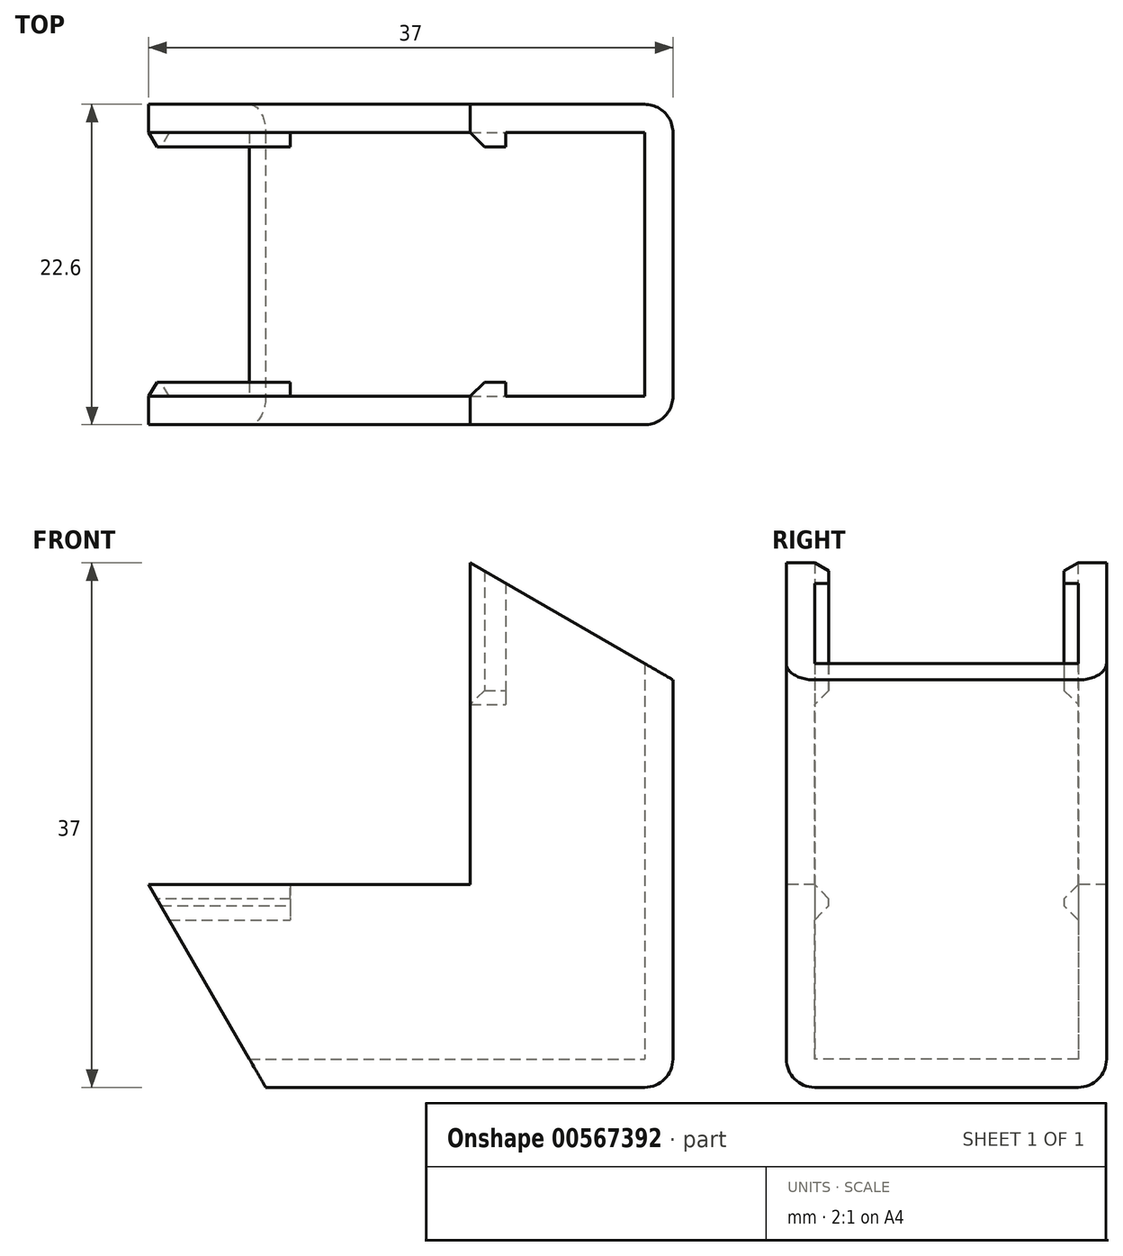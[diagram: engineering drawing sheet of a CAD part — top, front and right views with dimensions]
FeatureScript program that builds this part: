
annotation { "Feature Type Name" : "Feature", "Feature Type Description" : "" }
export const myFeature = defineFeature(function(context is Context, id is Id, definition is map)
    precondition{}
    {
        {
            assignVariable(context, id + "F0", {"name" : "Thickness", "anyValue" : 2});
        }
        {
            assignVariable(context, id + "F1", {"name" : "InsideWidth", "anyValue" : 18.6});
        }
        {
            assignVariable(context, id + "F2", {"name" : "OutsideLength", "anyValue" : 37});
        }
        {
            assignVariable(context, id + "F3", {"name" : "InsideDepth", "anyValue" : 12.3});
        }
        {
            var Q0;
            Q0=qCreatedBy(makeId("Top.planeOp"),FACE);
            var sketch = newSketch(context, id + "F4", { "sketchPlane" : qUnion([Q0])});
            skLineSegment(sketch, "E0.bottom", {"start": v(0, 0) * mm, "end": v(35, 0) * mm});
            skLineSegment(sketch, "E0.top", {"start": v(0, -22.6) * mm, "end": v(35, -22.6) * mm});
            skLineSegment(sketch, "E0.left", {"start": v(0, 0) * mm, "end": v(0, -22.6) * mm});
            skLineSegment(sketch, "E0.right", {"start": v(35, 0) * mm, "end": v(35, -22.6) * mm});
            skLineSegment(sketch, "E1.bottom", {"start": v(35, 0) * mm, "end": v(37, 0) * mm});
            skLineSegment(sketch, "E1.top", {"start": v(35, -22.6) * mm, "end": v(37, -22.6) * mm});
            skLineSegment(sketch, "E1.right", {"start": v(37, 0) * mm, "end": v(37, -22.6) * mm});
            skLineSegment(sketch, "E2", {"start": v(0, -11.3) * mm, "end": v(37, -11.3) * mm, "construction": true});
            skLineSegment(sketch, "E3", {"start": v(37, -2) * mm, "end": v(0, -2) * mm});
            skLineSegment(sketch, "E4", {"start": v(0, -20.6) * mm, "end": v(37, -20.6) * mm});
            skSolve(sketch);
        }
        {
            var Q0;
            {var subQ0=sQuery(id+"F4.wireOp",EDGE,"E3");var subQ1=sQuery(id+"F4.wireOp",EDGE,"E0.left");var subQ2=makeQuery(id+"F4.imprint","INTERSECT",VERTEX,{"derivedFrom":[subQ1,subQ0]});Q0=makeQuery(id+"F4.imprint","IMPRINT",FACE,{"disambiguationData":[TD([[makeQuery(id+"F4.imprint","IMPRINT",EDGE,{"disambiguationData":[TD([[subQ2,-1.0]])],"derivedFrom":subQ1}),1.0]])]});}
            extrude(context, id + "F5", {"entities" : qUnion([Q0]), "depth" : (getVariable(context, 'Thickness')) * mm, "offsetDistance" : 25 * mm});
        }
        {
            var Q0;
            {var subQ0=sQuery(id+"F4.wireOp",EDGE,"E3");var subQ1=sQuery(id+"F4.wireOp",EDGE,"E0.right");var subQ2=makeQuery(id+"F4.imprint","INTERSECT",VERTEX,{"derivedFrom":[subQ1,subQ0]});Q0=makeQuery(id+"F4.imprint","IMPRINT",FACE,{"disambiguationData":[TD([[makeQuery(id+"F4.imprint","IMPRINT",EDGE,{"disambiguationData":[TD([[subQ2,-1.0]])],"derivedFrom":subQ1}),1.0]])]});}
            var Q1;
            {var subQ0=sQuery(id+"F4.wireOp",EDGE,"E1.top");Q1=makeQuery(id+"F4.imprint","IMPRINT",FACE,{"disambiguationData":[TD([[makeQuery(id+"F4.imprint","IMPRINT",EDGE,{"derivedFrom":subQ0}),1.0]])]});}
            var Q2;
            {var subQ0=sQuery(id+"F4.wireOp",EDGE,"E1.bottom");Q2=makeQuery(id+"F4.imprint","IMPRINT",FACE,{"disambiguationData":[TD([[makeQuery(id+"F4.imprint","IMPRINT",EDGE,{"derivedFrom":subQ0}),-1.0]])]});}
            extrude(context, id + "F6", {"entities" : qUnion([Q0, Q1, Q2]), "operationType" : NewBodyOperationType.ADD, "depth" : (getVariable(context, 'OutsideLength')) * mm, "offsetDistance" : 25 * mm});
        }
        {
            var Q0;
            {var subQ0=sQuery(id+"F4.wireOp",EDGE,"E0.bottom");Q0=makeQuery(id+"F4.imprint","IMPRINT",FACE,{"disambiguationData":[TD([[makeQuery(id+"F4.imprint","IMPRINT",EDGE,{"derivedFrom":subQ0}),-1.0]])]});}
            var Q1;
            {var subQ0=sQuery(id+"F4.wireOp",EDGE,"E0.top");Q1=makeQuery(id+"F4.imprint","IMPRINT",FACE,{"disambiguationData":[TD([[makeQuery(id+"F4.imprint","IMPRINT",EDGE,{"derivedFrom":subQ0}),1.0]])]});}
            extrude(context, id + "F7", {"entities" : qUnion([Q0, Q1]), "operationType" : NewBodyOperationType.ADD, "depth" : (getVariable(context, 'InsideDepth') + getVariable(context, 'Thickness')) * mm, "offsetDistance" : 25 * mm});
        }
        {
            var Q0;
            Q0=makeQuery(id+"F6.opExtrude","SWEPT_FACE",FACE,{"disambiguationData":[OSD([sQuery(id+"F4.wireOp",EDGE,"E0.right")])]});
            var sketch = newSketch(context, id + "F8", { "sketchPlane" : qUnion([Q0])});
            skPoint(sketch, "E5.0", {"position": v(2, 14.3) * mm});
            skLineSegment(sketch, "E5.1", {"start": v(0, 14.3) * mm, "end": v(2, 14.3) * mm});
            skLineSegment(sketch, "E5.2", {"start": v(0, 37) * mm, "end": v(0, 14.3) * mm});
            skLineSegment(sketch, "E5.3", {"start": v(22.6, 37) * mm, "end": v(22.6, 14.3) * mm});
            skLineSegment(sketch, "E5.4", {"start": v(20.6, 14.3) * mm, "end": v(22.6, 14.3) * mm});
            skLineSegment(sketch, "E5.5", {"start": v(0, 37) * mm, "end": v(22.6, 37) * mm});
            skLineSegment(sketch, "E6", {"start": v(2, 14.3) * mm, "end": v(2, 37) * mm});
            skLineSegment(sketch, "E7", {"start": v(20.6, 14.3) * mm, "end": v(20.6, 37) * mm});
            skSolve(sketch);
        }
        {
            var Q0;
            Q0=makeQuery(id+"F8.imprint","IMPRINT",FACE,{"disambiguationData":[TD([[makeQuery(id+"F8.imprint","IMPRINT",EDGE,{"derivedFrom":sQuery(id+"F8.wireOp",EDGE,"E5.1")}),1.0]])]});
            var Q1;
            {var subQ0=sQuery(id+"F8.wireOp",EDGE,"E5.3");Q1=makeQuery(id+"F8.imprint","IMPRINT",FACE,{"disambiguationData":[TD([[makeQuery(id+"F8.imprint","IMPRINT",EDGE,{"derivedFrom":subQ0}),-1.0]])]});}
            extrude(context, id + "F9", {"entities" : qUnion([Q0, Q1]), "operationType" : NewBodyOperationType.ADD, "depth" : (getVariable(context, 'InsideDepth')) * mm, "offsetDistance" : 25 * mm});
        }
        {
            var Q0;
            Q0=makeQuery(id+"F9.boolean.opBoolean","MERGE",FACE,{"derivedFrom":[makeQuery(id+"F7.boolean.opBoolean","MERGE",FACE,{"derivedFrom":[makeQuery(id+"F6.opExtrude","SWEPT_FACE",FACE,{"disambiguationData":[OSD([sQuery(id+"F4.wireOp",EDGE,"E1.top")])]}),makeQuery(id+"F7.opExtrude","SWEPT_FACE",FACE,{"disambiguationData":[OSD([sQuery(id+"F4.wireOp",EDGE,"E0.top")])]})]}),makeQuery(id+"F9.opExtrude","SWEPT_FACE",FACE,{"disambiguationData":[OSD([sQuery(id+"F8.wireOp",EDGE,"E5.3")])]})]});
            var sketch = newSketch(context, id + "F10", { "sketchPlane" : qUnion([Q0])});
            skLineSegment(sketch, "E8", {"start": v(0, 14.3) * mm, "end": v(8.26, 0) * mm});
            skLineSegment(sketch, "E9", {"start": v(22.7, 37) * mm, "end": v(37, 28.74) * mm});
            skSolve(sketch);
        }
        {
            var Q0;
            {var subQ0=sQuery(id+"F10.wireOp",EDGE,"E8");Q0=makeQuery(id+"F10.imprint","IMPRINT",FACE,{"disambiguationData":[TD([[makeQuery(id+"F10.imprint","IMPRINT",EDGE,{"derivedFrom":subQ0}),-1.0]])]});}
            var Q1;
            {var subQ0=sQuery(id+"F10.wireOp",EDGE,"E9");Q1=makeQuery(id+"F10.imprint","IMPRINT",FACE,{"disambiguationData":[TD([[makeQuery(id+"F10.imprint","IMPRINT",EDGE,{"derivedFrom":subQ0}),1.0]])]});}
            extrude(context, id + "F11", {"entities" : qUnion([Q0, Q1]), "operationType" : NewBodyOperationType.REMOVE, "oppositeDirection" : true, "depth" : (getVariable(context, 'InsideWidth') + 2 * getVariable(context, 'Thickness')) * mm, "offsetDistance" : 25 * mm});
        }
        {
            var Q0;
            Q0=makeQuery(id+"F6.opExtrude","CAP_EDGE",EDGE,{"disambiguationData":[OSD([sQuery(id+"F4.wireOp",EDGE,"E1.right")])],"isStart":true});
            var Q1;
            Q1=makeQuery(id+"F7.boolean.opBoolean","MERGE",EDGE,{"derivedFrom":[makeQuery(id+"F6.opExtrude","CAP_EDGE",EDGE,{"disambiguationData":[OSD([sQuery(id+"F4.wireOp",EDGE,"E1.top")])],"isStart":true}),makeQuery(id+"F7.opExtrude","CAP_EDGE",EDGE,{"disambiguationData":[OSD([sQuery(id+"F4.wireOp",EDGE,"E0.top")])],"isStart":true})]});
            var Q2;
            Q2=makeQuery(id+"F6.opExtrude","SWEPT_EDGE",EDGE,{"disambiguationData":[OSD([sQuery(id+"F4.wireOp",EDGE,"E1.top"),sQuery(id+"F4.wireOp",EDGE,"E1.right")])]});
            var Q3;
            Q3=makeQuery(id+"F6.opExtrude","SWEPT_EDGE",EDGE,{"disambiguationData":[OSD([sQuery(id+"F4.wireOp",EDGE,"E1.bottom"),sQuery(id+"F4.wireOp",EDGE,"E1.right")])]});
            var Q4;
            Q4=makeQuery(id+"F7.boolean.opBoolean","MERGE",EDGE,{"derivedFrom":[makeQuery(id+"F6.opExtrude","CAP_EDGE",EDGE,{"disambiguationData":[OSD([sQuery(id+"F4.wireOp",EDGE,"E1.bottom")])],"isStart":true}),makeQuery(id+"F7.opExtrude","CAP_EDGE",EDGE,{"disambiguationData":[OSD([sQuery(id+"F4.wireOp",EDGE,"E0.bottom")])],"isStart":true})]});
            var Q5;
            Q5=makeQuery(id+"F11.boolean.opBoolean","COPY",EDGE,{"derivedFrom":makeQuery(id+"F11.opExtrude","SWEPT_EDGE",EDGE,{"disambiguationData":[OSD([sQuery(id+"F4.wireOp",EDGE,"E0.top"),sQuery(id+"F4.wireOp",EDGE,"E1.top"),sQuery(id+"F10.wireOp",EDGE,"E8")])]})});
            var Q6;
            Q6=makeQuery(id+"F11.boolean.opBoolean","COPY",EDGE,{"derivedFrom":makeQuery(id+"F11.opExtrude","SWEPT_EDGE",EDGE,{"disambiguationData":[OSD([sQuery(id+"F4.wireOp",EDGE,"E1.top"),sQuery(id+"F4.wireOp",EDGE,"E1.right"),sQuery(id+"F10.wireOp",EDGE,"E9")])]})});
            fillet(context, id + "F12", {"entities" : qUnion([Q0, Q1, Q2, Q3, Q4, Q5, Q6]), "radius" : (getVariable(context, 'Thickness')) * mm, "tangentPropagation" : true, "allowEdgeOverflow" : false});
        }
        {
            var Q0;
            Q0=makeQuery(id+"F9.boolean.opBoolean","MERGE",FACE,{"derivedFrom":[makeQuery(id+"F7.opExtrude","SWEPT_FACE",FACE,{"disambiguationData":[OSD([sQuery(id+"F4.wireOp",EDGE,"E3")])]}),makeQuery(id+"F9.opExtrude","SWEPT_FACE",FACE,{"disambiguationData":[OSD([sQuery(id+"F8.wireOp",EDGE,"E6")])]})]});
            var sketch = newSketch(context, id + "F13", { "sketchPlane" : qUnion([Q0])});
            skLineSegment(sketch, "E10.bottom", {"start": v(22.7, 37) * mm, "end": v(25.2, 37) * mm});
            skLineSegment(sketch, "E10.top", {"start": v(22.7, 27) * mm, "end": v(25.2, 27) * mm});
            skLineSegment(sketch, "E10.left", {"start": v(22.7, 37) * mm, "end": v(22.7, 27) * mm});
            skLineSegment(sketch, "E10.right", {"start": v(25.2, 37) * mm, "end": v(25.2, 27) * mm});
            skLineSegment(sketch, "E11.bottom", {"start": v(0, 14.3) * mm, "end": v(10, 14.3) * mm});
            skLineSegment(sketch, "E11.top", {"start": v(0, 11.8) * mm, "end": v(10, 11.8) * mm});
            skLineSegment(sketch, "E11.left", {"start": v(0, 14.3) * mm, "end": v(0, 11.8) * mm});
            skLineSegment(sketch, "E11.right", {"start": v(10, 14.3) * mm, "end": v(10, 11.8) * mm});
            skSolve(sketch);
        }
        {
            var Q0;
            {var subQ0=sQuery(id+"F13.wireOp",EDGE,"E10.top");Q0=makeQuery(id+"F13.imprint","IMPRINT",FACE,{"disambiguationData":[TD([[makeQuery(id+"F13.imprint","IMPRINT",EDGE,{"derivedFrom":subQ0}),1.0]])]});}
            var Q1;
            {var subQ0=sQuery(id+"F13.wireOp",EDGE,"E11.bottom");Q1=makeQuery(id+"F13.imprint","IMPRINT",FACE,{"disambiguationData":[TD([[makeQuery(id+"F13.imprint","IMPRINT",EDGE,{"derivedFrom":subQ0}),1.0]])]});}
            extrude(context, id + "F14", {"entities" : qUnion([Q0, Q1]), "operationType" : NewBodyOperationType.ADD, "depth" : 1 * mm, "offsetDistance" : 25 * mm});
        }
        {
            var Q0;
            Q0=makeQuery(id+"F14.opExtrude","CAP_EDGE",EDGE,{"disambiguationData":[OSD([sQuery(id+"F13.wireOp",EDGE,"E10.top")])],"isStart":false});
            var Q1;
            Q1=makeQuery(id+"F14.opExtrude","CAP_EDGE",EDGE,{"disambiguationData":[OSD([sQuery(id+"F13.wireOp",EDGE,"E11.top")])],"isStart":false});
            var Q2;
            Q2=makeQuery(id+"F14.opExtrude","CAP_EDGE",EDGE,{"disambiguationData":[OSD([sQuery(id+"F13.wireOp",EDGE,"E10.left")])],"isStart":false});
            var Q3;
            Q3=makeQuery(id+"F14.opExtrude","CAP_EDGE",EDGE,{"disambiguationData":[OSD([sQuery(id+"F13.wireOp",EDGE,"E11.bottom")])],"isStart":false});
            chamfer(context, id + "F15", {"entities" : qUnion([Q0, Q1, Q2, Q3]), "width" : 1 * mm, "tangentPropagation" : true});
        }
        {
            var Q0;
            Q0=makeQuery(id+"F9.boolean.opBoolean","MERGE",FACE,{"derivedFrom":[makeQuery(id+"F7.opExtrude","SWEPT_FACE",FACE,{"disambiguationData":[OSD([sQuery(id+"F4.wireOp",EDGE,"E4")])]}),makeQuery(id+"F9.opExtrude","SWEPT_FACE",FACE,{"disambiguationData":[OSD([sQuery(id+"F8.wireOp",EDGE,"E7")])]})]});
            var sketch = newSketch(context, id + "F16", { "sketchPlane" : qUnion([Q0])});
            skLineSegment(sketch, "E12.bottom", {"start": v(-22.7, 37) * mm, "end": v(-25.2, 37) * mm});
            skLineSegment(sketch, "E12.top", {"start": v(-22.7, 27) * mm, "end": v(-25.2, 27) * mm});
            skLineSegment(sketch, "E12.left", {"start": v(-22.7, 37) * mm, "end": v(-22.7, 27) * mm});
            skLineSegment(sketch, "E12.right", {"start": v(-25.2, 37) * mm, "end": v(-25.2, 27) * mm});
            skLineSegment(sketch, "E13.bottom", {"start": v(0, 14.3) * mm, "end": v(-10, 14.3) * mm});
            skLineSegment(sketch, "E13.top", {"start": v(0, 11.8) * mm, "end": v(-10, 11.8) * mm});
            skLineSegment(sketch, "E13.left", {"start": v(0, 14.3) * mm, "end": v(0, 11.8) * mm});
            skLineSegment(sketch, "E13.right", {"start": v(-10, 14.3) * mm, "end": v(-10, 11.8) * mm});
            skSolve(sketch);
        }
        {
            var Q0;
            {var subQ0=sQuery(id+"F16.wireOp",EDGE,"E12.top");Q0=makeQuery(id+"F16.imprint","IMPRINT",FACE,{"disambiguationData":[TD([[makeQuery(id+"F16.imprint","IMPRINT",EDGE,{"derivedFrom":subQ0}),-1.0]])]});}
            var Q1;
            {var subQ0=sQuery(id+"F16.wireOp",EDGE,"E13.bottom");Q1=makeQuery(id+"F16.imprint","IMPRINT",FACE,{"disambiguationData":[TD([[makeQuery(id+"F16.imprint","IMPRINT",EDGE,{"derivedFrom":subQ0}),1.0]])]});}
            extrude(context, id + "F17", {"entities" : qUnion([Q0, Q1]), "operationType" : NewBodyOperationType.ADD, "depth" : 1 * mm, "offsetDistance" : 25 * mm});
        }
        {
            var Q0;
            Q0=makeQuery(id+"F17.opExtrude","CAP_EDGE",EDGE,{"disambiguationData":[OSD([sQuery(id+"F16.wireOp",EDGE,"E13.top")])],"isStart":false});
            var Q1;
            Q1=makeQuery(id+"F17.opExtrude","CAP_EDGE",EDGE,{"disambiguationData":[OSD([sQuery(id+"F16.wireOp",EDGE,"E13.bottom")])],"isStart":false});
            var Q2;
            Q2=makeQuery(id+"F17.opExtrude","CAP_EDGE",EDGE,{"disambiguationData":[OSD([sQuery(id+"F16.wireOp",EDGE,"E12.left")])],"isStart":false});
            var Q3;
            Q3=makeQuery(id+"F17.opExtrude","CAP_EDGE",EDGE,{"disambiguationData":[OSD([sQuery(id+"F16.wireOp",EDGE,"E12.top")])],"isStart":false});
            chamfer(context, id + "F18", {"entities" : qUnion([Q0, Q1, Q2, Q3]), "width" : 1 * mm, "tangentPropagation" : true});
        }
    });
